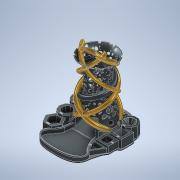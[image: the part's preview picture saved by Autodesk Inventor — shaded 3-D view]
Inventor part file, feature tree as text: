
AUTODESK INVENTOR PART (.ipt)
format: ipt  version: 2022 (Build 260153000, 153)  size: 7,636,992 bytes
history: native  units: mm
features: sketch x29, extrude x25, helix x5, fillet x4, plane x3, chamfer x3, revolve x2, pattern_circular x2
ambient origin geometry x8: Origin, YZ Plane, XZ Plane, XY Plane, X Axis, Y Axis, Z Axis, Center Point
bodies: Solid1 (feature_tree)
feature tree (73):
  revolve  "Revolution1"  [1 undecoded]
  plane  "Work Plane1"
  extrude  "Extrusion4"  Depth=20.0mm
  extrude  "Extrusion2"  Depth=19.0mm
  pattern_circular  "Circular Pattern2"  Count=9  [1 undecoded]
  plane  "Work Plane3"
  extrude  "Extrusion3"  Depth=10.0mm
  pattern_circular  "Circular Pattern3"  Count=7  [1 undecoded]
  helix  "Coil1"  [1 undecoded]
  helix  "Coil2"  [1 undecoded]
  helix  "Coil3"  [1 undecoded]
  helix  "Coil4"  [1 undecoded]
  helix  "Coil5"  [1 undecoded]
  extrude  "Extrusion5"  Depth=20.0mm
  revolve  "Revolution2"  [1 undecoded]
  extrude  "Extrusion6"  Depth=30.0mm
  extrude  "Extrusion7"  Depth=15.0mm
  extrude  "Extrusion15"  Depth=30.0mm
  extrude  "Extrusion16"  Depth=45.0mm
  extrude  "Extrusion17"  Depth=13.0mm
  extrude  "Extrusion18"  Depth=39.0mm
  extrude  "Extrusion19"  Depth=11.0mm
  extrude  "Extrusion20"  Depth=10.0mm
  extrude  "Extrusion21"  Depth=11.0mm
  extrude  "Extrusion22"  Depth=9.0mm
  extrude  "Extrusion23"  Depth=3.0mm TaperAngle=0.0deg
  extrude  "Extrusion25"  Depth=60.0mm
  fillet  "Fillet3"  [1 undecoded]
  extrude  "Extrusion26"  Depth=54.0mm TaperAngle=0.0deg
  extrude  "Extrusion27"  Depth=35.0mm
  extrude  "Extrusion28"  Depth=30.0mm
  extrude  "Extrusion29"  Depth=30.0mm
  extrude  "Extrusion30"  Depth=35.0mm
  extrude  "Extrusion31"  Depth=35.0mm
  extrude  "Extrusion32"  Depth=5.0mm
  chamfer  "Chamfer1"  Distance=10.0mm
  extrude  "Extrusion33"  Depth=5.0mm TaperAngle=0.0deg
  chamfer  "Chamfer2"  Distance=10.0mm
  chamfer  "Chamfer3"  Distance=15.0mm
  fillet  "Fillet4"  Radius=0.2mm
  fillet  "Fillet5"  Radius=5.0mm
  fillet  "Fillet6"  Radius=10.0mm
  extrude  "Extrusion34"  Depth=15.0mm TaperAngle=0.0deg
  sketch  "Sketch1"  dims[d11=60.0mm d12=40.0mm]
  sketch  "Sketch3"  dims[d13=20.0mm d14=20.0mm]
  plane  "Work Plane2"
  sketch  "Sketch4"  dims[d15=20.0mm d16=19.0mm d17=90.0mm]
  sketch  "Sketch5"  dims[d18=30.0mm d19=10.0mm]
  sketch  "Sketch7"  dims[d20=149.0mm]
  sketch  "Sketch8"  dims[d26=2.0mm]
  sketch  "Sketch9"  dims[d27=2.0mm]
  sketch  "Sketch10"  dims[d28=2.0mm]
  sketch  "Sketch11"  dims[d29=2.0mm]
  sketch  "Sketch13"  dims[d30=2.0mm]
  sketch  "Sketch16"  dims[d31=90.0deg d32=70.0mm d38=77.75mm d39=0.0mm d40=40.0mm d41=360.0deg d43=70.0mm d44=77.75mm d45=0.0mm d46=40.0mm d47=360.0deg]
  sketch  "Sketch17"  dims[d49=20.0mm d50=20.0mm]
  sketch  "Sketch20"  dims[d51=20.0mm d52=20.0mm]
  sketch  "Sketch21"  dims[d53=40.0mm d54=30.0mm]
  sketch  "Sketch22"  dims[d55=30.0mm d56=15.0mm]
  sketch  "Sketch23"  dims[d57=15.0mm d58=30.0mm]
  sketch  "Sketch26"  dims[d59=77.75mm d60=0.0mm d61=45.0mm]
  sketch  "Sketch27"  dims[d62=35.0mm]
  sketch  "Sketch28"  dims[d63=70.0mm d64=100.0mm d65=10.0mm d66=-0.567232mm d67=90.0deg d68=90.0deg d69=90.0deg d70=90.0deg d71=13.0mm]
  sketch  "Sketch30"  dims[d72=10.0mm d73=39.0mm]
  sketch  "Sketch31"  dims[d74=140.0mm d75=160.0mm d76=10.0mm d77=-0.645772mm d78=90.0deg d79=90.0deg d80=90.0deg d81=90.0deg d82=11.0mm]
  sketch  "Sketch33"  dims[d83=39.0mm d84=10.0mm]
  sketch  "Sketch35"  dims[d85=135.0mm d86=160.0mm d87=10.0mm d88=-0.645772mm d89=90.0deg d90=90.0deg d91=90.0deg d92=90.0deg d93=11.0mm]
  sketch  "Sketch37"  dims[d94=170.0mm d95=160.0mm d96=10.0mm d97=-0.645772mm d98=90.0deg d99=90.0deg d100=90.0deg d101=90.0deg d102=9.0mm]
  sketch  "Sketch38"  dims[d103=170.0mm d104=160.0mm d105=10.0mm d106=-0.645772mm d107=90.0deg d108=90.0deg d109=90.0deg d110=90.0deg d125=3.0mm d126=0.0mm]
  sketch  "Sketch39"  dims[d128=60.0mm d129=43.0mm d130=270.0deg]
  sketch  "Sketch40"  dims[d132=34.0mm d133=54.0mm d134=0.0mm]
  sketch  "Sketch41"  dims[d136=54.0mm d137=0.0mm d141=35.0mm]
  sketch  "Sketch43"  dims[d165=35.0mm d166=30.0mm d167=30.0mm d168=30.0mm d169=30.0mm d170=35.0mm d172=35.0mm d186=5.0mm d187=10.0mm d188=0.0mm d190=5.0mm d191=0.0mm d192=10.0mm d193=0.0mm d194=15.0mm d195=0.0mm d196=0.2mm d197=0.0mm d198=5.0mm d199=0.0mm d200=10.0mm d201=0.0mm d202=15.0mm d203=0.0mm d204=3.0mm d205=0.0mm d210=1.0mm d211=0.0mm d212=3.6mm d213=10.0mm d214=0.0mm d215=20.0mm d216=24.0mm d217=20.0mm d218=30.0mm d219=23.5mm d220=5.75mm d221=5.75mm d222=5.75mm d223=14.0mm d224=0.0mm d225=22.5mm d226=6.25mm d227=6.25mm d228=6.25mm d229=14.0mm d230=0.0mm d231=25.0mm d232=5.0mm d233=5.0mm d234=5.0mm d235=14.0mm d236=0.0mm d237=25.5mm d239=3.0mm d241=10.0mm d242=0.0mm d243=54.0mm d244=43.0mm d245=17.5mm d246=17.5mm d247=7.0mm d248=5.5mm d249=4.0mm d250=3.607976mm d251=10.0mm d252=0.0mm d253=21.0mm d254=21.0mm d255=5.0mm d256=4.0mm d257=5.0mm d258=24.0mm d259=0.0mm d260=10.0mm d261=2.0mm d262=45.0deg d263=25.0mm d266=5.0mm d267=5.0mm d268=12.0mm d269=0.0mm d270=11.0mm d271=2.0mm d272=45.0deg d273=12.0mm d274=2.0mm d275=45.0deg d276=35.0mm d277=3.0mm d278=5.0mm d279=5.0mm d280=5.0mm d281=2.0mm d282=2.0mm d283=1.56mm d292=20.0mm d293=0.0mm d135=0.0mm]
note: 10 required parameter values undecoded (feature->parameter linkage not recoverable at this tier; creation-order binding heuristic only, values carry confidence <= 0.55)